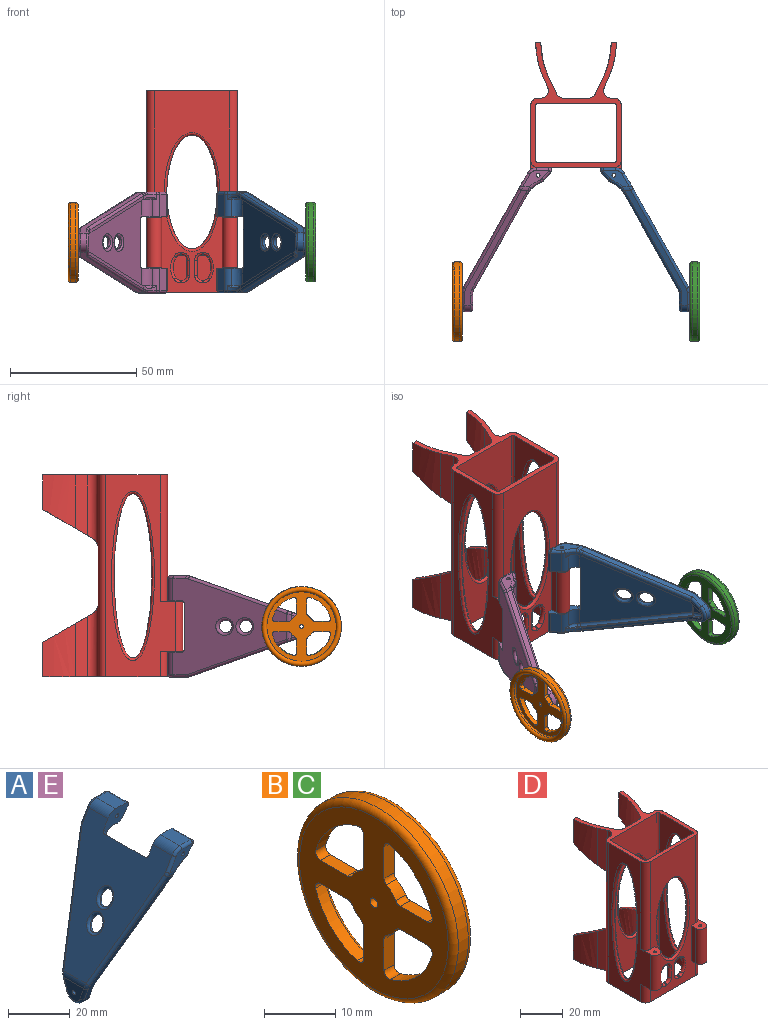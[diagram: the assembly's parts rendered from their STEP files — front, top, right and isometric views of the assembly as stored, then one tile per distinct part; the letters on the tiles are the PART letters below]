
ASSEMBLY  parts=5 mates=6
PART A: 94 faces, bbox 35.6x40.5x58 mm
  f0: cylinder r=3mm len=8.75mm, axis (0,1,0), area 25.5mm2, adj f1,f25,f29,f32,f38,f85
  f1: plane 8.75x3.29mm, normal (0.77,0,-0.64), area 37.5mm2, adj f0,f25,f52,f83
  f2: plane 8.75x4.95mm, normal (0,0,1), area 43.3mm2, adj f25,f31,f52,f79
  f3: cylinder r=3mm len=8.75mm, axis (0,1,0), area 25.5mm2, adj f4,f24,f28,f30,f40,f76
  f4: plane 8.75x3.29mm, normal (0.77,0,-0.64), area 37.5mm2, adj f3,f24,f55,f74
  f5: plane 8.75x4.95mm, normal (0,0,1), area 43.3mm2, adj f24,f37,f55,f70
  f6: plane 10.42x6.61mm, normal (0,-1,0), area 31.7mm2, adj f27,f34,f66,f68,f70,f74,f76,f78
  f7: plane 10.42x6.61mm, normal (0,1,0), area 31.7mm2, adj f26,f33,f75,f77,f79,f83,f85,f87
  f8: plane 40.52x33.68mm, normal (0.87,0,-0.49), area 800.5mm2, adj f23,f30,f32,f43,f46,f47,f53,f54
  f9: plane 37.92x21.33mm, normal (0.87,0,-0.49), area 53.6mm2, adj f22,f28,f36,f84
  f10: plane 38.87x21.87mm, normal (0.87,0,-0.49), area 54.9mm2, adj f11,f20,f29,f92,f93
  f11: plane 8.76x6.93mm, normal (1,0,0), area 15.1mm2, adj f10,f20,f21,f22,f36,f88,f90,f92
  f12: plane 45.38x38.33mm, normal (-0.87,0,0.49), area 1142.3mm2, adj f23,f24,f25,f31,f35,f37,f53,f54
  f13: plane 9.15x6.95mm, normal (-1,0,0), area 43.1mm2, adj f35,f56,f63,f65,f67
  f14: plane 45.39x24.79mm, normal (0,0.94,-0.33), area 113.4mm2, adj f15,f33,f67,f69,f71,f91,f92,f93
  f15: cylinder r=4mm len=7.55mm, axis (1,0,0), area 20.6mm2, adj f14,f16,f65,f90
  f16: plane 45.39x24.79mm, normal (0,-0.94,-0.33), area 113.5mm2, adj f15,f34,f61,f62,f63,f82,f84,f86
  f17: plane 2.99x1.2mm, normal (0,1,0), area 1.9mm2, adj f22,f28,f42,f44
  f18: plane 2.99x1.2mm, normal (0,-1,0), area 1.9mm2, adj f20,f29,f39,f41
  f19: plane 5.21x5.09mm, normal (1,0,0), area 15mm2, adj f47,f48,f50,f51,f56
  f20: plane 45.75x24.74mm, normal (0,-0.94,0.33), area 51.8mm2, adj f10,f11,f18,f21,f29,f41,f43,f48
  f21: cylinder r=2mm len=3.77mm, axis (1,0,0), area 5.3mm2, adj f11,f20,f22,f50
  f22: plane 45.75x24.74mm, normal (0,0.94,0.33), area 51.9mm2, adj f9,f11,f17,f21,f28,f36,f44,f46
  f23: cylinder r=7.5mm len=18.5mm, axis (0,1,0), area 40.8mm2, adj f8,f12,f53,f54
  f24: plane 11.33x7.37mm, normal (0,1,0), area 49mm2, adj f3,f4,f5,f12,f27,f30,f37,f54
  f25: plane 11.33x7.37mm, normal (0,-1,0), area 49mm2, adj f0,f1,f2,f12,f26,f31,f32,f52
  f26: cylinder r=0.75mm len=9.75mm, axis (0,-1,0), area 45.9mm2, adj f7,f25
  f27: cylinder r=0.75mm len=9.75mm, axis (0,-1,0), area 45.9mm2, adj f6,f24
  f28: cylinder r=10mm len=5.14mm, axis (0,1,0), area 8.4mm2, adj f3,f9,f17,f22,f40,f42,f78,f80
  f29: cylinder r=10mm len=5.14mm, axis (0,1,0), area 8.4mm2, adj f0,f10,f18,f20,f38,f39,f87,f89
  f30: cylinder r=4mm len=6.91mm, axis (0,1,0), area 34.9mm2, adj f3,f8,f24,f42,f44,f54
  f31: cylinder r=4mm len=8.75mm, axis (0,1,0), area 37mm2, adj f2,f12,f25,f77
  f32: cylinder r=4mm len=6.91mm, axis (0,1,0), area 34.9mm2, adj f0,f8,f25,f39,f41,f53
  f33: cylinder r=4mm len=3.32mm, axis (1,0,0), area 3.6mm2, adj f7,f14,f73,f89
  f34: cylinder r=4mm len=3.32mm, axis (-1,0,0), area 3.6mm2, adj f6,f16,f64,f80
  f35: cylinder r=4mm len=10.19mm, axis (0,1,0), area 19.8mm2, adj f12,f13,f61,f69
  f36: cylinder r=4mm len=1.96mm, axis (0,-1,0), area 2.4mm2, adj f9,f11,f22,f86
  f37: cylinder r=4mm len=8.75mm, axis (0,1,0), area 37mm2, adj f5,f12,f24,f68
  f38: torus R=4mm, axis (0,-1,0), area 1.4mm2, adj f0,f29,f39
  f39: torus R=3mm, axis (0,-1,0), area 6.2mm2, adj f18,f29,f32,f38,f41
  f40: torus R=4mm, axis (0,-1,0), area 1.4mm2, adj f3,f28,f42
  f41: bspline ~2.59x2.16mm, area 1.7mm2, adj f18,f20,f32,f39,f43
  f42: torus R=3mm, axis (0,-1,0), area 6.2mm2, adj f17,f28,f30,f40,f44
  f43: cylinder r=1mm len=41.27mm, axis (0.47,0.29,0.83), area 84.2mm2, adj f8,f20,f41,f45
  f44: bspline ~2.59x2.16mm, area 1.7mm2, adj f17,f22,f30,f42,f46
  f45: sphere r=1mm, area 0.4mm2, adj f43,f47,f48
  f46: cylinder r=1mm len=41.27mm, axis (-0.47,0.29,-0.83), area 84.2mm2, adj f8,f22,f44,f49
  f47: cylinder r=1mm len=5.09mm, axis (0,-1,0), area 2.6mm2, adj f8,f19,f45,f49
  f48: cylinder r=1mm len=4.88mm, axis (0,0.33,0.94), area 7.6mm2, adj f19,f20,f45,f50
  f49: sphere r=1mm, area 0.4mm2, adj f46,f47,f51
  f50: torus R=1mm, axis (-1,0,0), area 6.3mm2, adj f19,f21,f48,f51
  f51: cylinder r=1mm len=4.88mm, axis (0,0.33,-0.94), area 7.6mm2, adj f19,f22,f49,f50
  f52: cylinder r=1mm len=8.75mm, axis (0,1,0), area 19.9mm2, adj f1,f2,f25,f81
  f53: torus R=6.5mm, axis (0,-1,0), area 3.7mm2, adj f8,f12,f23,f25,f32
  f54: torus R=6.5mm, axis (0,-1,0), area 3.7mm2, adj f8,f12,f23,f24,f30
  f55: cylinder r=1mm len=8.75mm, axis (0,1,0), area 19.9mm2, adj f4,f5,f24,f72
  f56: cylinder r=0.75mm len=2mm, axis (-1,0,0), area 9.4mm2, adj f13,f19
  f57: bspline ~7x7mm, area 30.8mm2, adj f12,f58
  f58: bspline ~7x6.99mm, area 30.9mm2, adj f8,f57
  f59: bspline ~7x7mm, area 30.8mm2, adj f12,f60
  f60: bspline ~7x6.99mm, area 30.9mm2, adj f8,f59
  f61: bspline ~2.29x1.46mm, area 3.2mm2, adj f16,f35,f62,f63
  f62: cylinder r=1mm len=39.79mm, axis (0.47,-0.29,0.83), area 81.1mm2, adj f12,f16,f61,f64
  f63: cylinder r=1mm len=5.28mm, axis (0,-0.33,0.94), area 8.2mm2, adj f13,f16,f61,f65
  f64: bspline ~2.83x2.1mm, area 2.2mm2, adj f12,f34,f62,f66
  f65: torus R=3mm, axis (-1,0,0), area 14.1mm2, adj f13,f15,f63,f67
  f66: cylinder r=1mm len=5.57mm, axis (0.49,0,0.87), area 9.2mm2, adj f6,f12,f64,f68
  f67: cylinder r=1mm len=5.28mm, axis (0,-0.33,-0.94), area 8.2mm2, adj f13,f14,f65,f69
  f68: torus R=3mm, axis (0,-1,0), area 6mm2, adj f6,f37,f66,f70
  f69: bspline ~2.29x1.46mm, area 3.2mm2, adj f14,f35,f67,f71
  f70: cylinder r=1mm len=4.95mm, axis (1,0,0), area 7.8mm2, adj f5,f6,f68,f72
  f71: cylinder r=1mm len=39.79mm, axis (-0.47,-0.29,-0.83), area 81.1mm2, adj f12,f14,f69,f73
  f72: sphere r=1mm, area 2.6mm2, adj f55,f70,f74
  f73: bspline ~2.83x2.1mm, area 2.2mm2, adj f12,f33,f71,f75
  f74: cylinder r=1mm len=3.93mm, axis (-0.64,0,-0.77), area 6.7mm2, adj f4,f6,f72,f76
  f75: cylinder r=1mm len=5.57mm, axis (-0.49,0,-0.87), area 9.2mm2, adj f7,f12,f73,f77
  f76: torus R=2mm, axis (0,-1,0), area 2.1mm2, adj f3,f6,f74,f78
  f77: torus R=3mm, axis (0,-1,0), area 6mm2, adj f7,f31,f75,f79
  f78: torus R=11mm, axis (0,-1,0), area 7.4mm2, adj f6,f28,f76,f80
  f79: cylinder r=1mm len=4.95mm, axis (-1,0,0), area 7.8mm2, adj f2,f7,f77,f81
  f80: bspline ~3.6x2.99mm, area 2.1mm2, adj f28,f34,f78,f82
  f81: sphere r=1mm, area 2.6mm2, adj f52,f79,f83
  f82: bspline ~1.54x1.36mm, area 1.9mm2, adj f16,f28,f80,f84
  f83: cylinder r=1mm len=3.93mm, axis (0.64,0,0.77), area 6.7mm2, adj f1,f7,f81,f85
  f84: cylinder r=1mm len=38.14mm, axis (-0.47,0.29,-0.83), area 64mm2, adj f9,f16,f82,f86
  f85: torus R=2mm, axis (0,-1,0), area 2.1mm2, adj f0,f7,f83,f87
  f86: bspline ~3.56x2.2mm, area 3.6mm2, adj f16,f36,f84,f88
  f87: torus R=11mm, axis (0,-1,0), area 7.4mm2, adj f7,f29,f85,f89
  f88: cylinder r=1mm len=4.21mm, axis (0,0.33,-0.94), area 6.5mm2, adj f11,f16,f86,f90
  f89: bspline ~3.6x2.99mm, area 2.1mm2, adj f29,f33,f87,f91
  f90: torus R=3mm, axis (1,0,0), area 14.1mm2, adj f11,f15,f88,f92
  f91: bspline ~1.54x1.36mm, area 1.9mm2, adj f14,f29,f89,f93
  f92: cylinder r=1mm len=5.52mm, axis (0,0.33,0.94), area 8.4mm2, adj f10,f11,f14,f90,f93
  f93: cylinder r=1mm len=39.28mm, axis (0.47,0.29,0.83), area 65.8mm2, adj f10,f14,f91,f92
PART B: 39 faces, bbox 4x34.1x34.1 mm
  f0: plane 29.5x29.5mm, normal (-1,0,0), area 424.6mm2, adj f2,f5,f7,f8,f9,f10,f11,f12
  f1: cylinder r=15.75mm len=31.5mm, axis (-1,0,0), area 197.9mm2, adj f5,f6
  f2: cylinder r=0.75mm len=2mm, axis (-1,0,0), area 9.4mm2, adj f0,f3
  f3: plane 27.5x27.5mm, normal (1,0,0), area 335.1mm2, adj f2,f4,f7,f8,f9,f10,f11,f12
  f4: cylinder r=13.75mm len=27.5mm, axis (-1,0,0), area 86.4mm2, adj f3,f6
  f5: torus R=14.75mm, axis (1,0,0), area 151.9mm2, adj f0,f1
  f6: torus R=14.75mm, axis (1,0,0), area 291.2mm2, adj f1,f4
  f7: plane 5.39x2mm, normal (0,-1,0), area 10.8mm2, adj f0,f3,f11,f14
  f8: cylinder r=5mm len=2mm, axis (1,0,0), area 5.2mm2, adj f0,f3,f11,f12
  f9: plane 5.39x2mm, normal (0,0,-1), area 10.8mm2, adj f0,f3,f12,f13
  f10: cylinder r=12mm len=8.27mm, axis (1,0,0), area 24.4mm2, adj f0,f3,f13,f14
  f11: cylinder r=1mm len=2mm, axis (1,0,0), area 2.1mm2, adj f0,f3,f7,f8
  f12: cylinder r=1mm len=2mm, axis (1,0,0), area 2.1mm2, adj f0,f3,f8,f9
  f13: cylinder r=1mm len=2mm, axis (1,0,0), area 3.7mm2, adj f0,f3,f9,f10
  f14: cylinder r=1mm len=2mm, axis (1,0,0), area 3.7mm2, adj f0,f3,f7,f10
  f15: plane 5.39x2mm, normal (0,0,1), area 10.8mm2, adj f0,f3,f19,f22
  f16: cylinder r=5mm len=2mm, axis (1,0,0), area 5.2mm2, adj f0,f3,f19,f20
  f17: plane 5.39x2mm, normal (0,-1,0), area 10.8mm2, adj f0,f3,f20,f21
  f18: cylinder r=12mm len=8.27mm, axis (1,0,0), area 24.4mm2, adj f0,f3,f21,f22
  f19: cylinder r=1mm len=2mm, axis (1,0,0), area 2.1mm2, adj f0,f3,f15,f16
  f20: cylinder r=1mm len=2mm, axis (1,0,0), area 2.1mm2, adj f0,f3,f16,f17
  f21: cylinder r=1mm len=2mm, axis (1,0,0), area 3.7mm2, adj f0,f3,f17,f18
  f22: cylinder r=1mm len=2mm, axis (1,0,0), area 3.7mm2, adj f0,f3,f15,f18
  f23: plane 5.39x2mm, normal (0,1,0), area 10.8mm2, adj f0,f3,f27,f30
  f24: cylinder r=5mm len=2mm, axis (1,0,0), area 5.2mm2, adj f0,f3,f27,f28
  f25: plane 5.39x2mm, normal (0,0,1), area 10.8mm2, adj f0,f3,f28,f29
  f26: cylinder r=12mm len=8.27mm, axis (1,0,0), area 24.4mm2, adj f0,f3,f29,f30
  f27: cylinder r=1mm len=2mm, axis (1,0,0), area 2.1mm2, adj f0,f3,f23,f24
  f28: cylinder r=1mm len=2mm, axis (1,0,0), area 2.1mm2, adj f0,f3,f24,f25
  f29: cylinder r=1mm len=2mm, axis (1,0,0), area 3.7mm2, adj f0,f3,f25,f26
  f30: cylinder r=1mm len=2mm, axis (1,0,0), area 3.7mm2, adj f0,f3,f23,f26
  f31: plane 5.39x2mm, normal (0,0,-1), area 10.8mm2, adj f0,f3,f35,f38
  f32: cylinder r=5mm len=2mm, axis (1,0,0), area 5.2mm2, adj f0,f3,f35,f36
  f33: plane 5.39x2mm, normal (0,1,0), area 10.8mm2, adj f0,f3,f36,f37
  f34: cylinder r=12mm len=8.27mm, axis (1,0,0), area 24.4mm2, adj f0,f3,f37,f38
  f35: cylinder r=1mm len=2mm, axis (1,0,0), area 2.1mm2, adj f0,f3,f31,f32
  f36: cylinder r=1mm len=2mm, axis (1,0,0), area 2.1mm2, adj f0,f3,f32,f33
  f37: cylinder r=1mm len=2mm, axis (1,0,0), area 3.7mm2, adj f0,f3,f33,f34
  f38: cylinder r=1mm len=2mm, axis (1,0,0), area 3.7mm2, adj f0,f3,f31,f34
PART C: same geometry as B
PART D: 100 faces, bbox 36.6x56.1x80.6 mm
  f0: extruded ~40.69x5.73mm, area 52.2mm2, adj f26,f45,f49,f83,f86,f87
  f1: plane 80x30mm, normal (0,-1,0), area 1311.5mm2, adj f33,f34,f36,f38,f39,f41,f43,f44
  f2: plane 80x30mm, normal (0,1,0), area 1431.5mm2, adj f33,f34,f67,f68,f69,f70,f71,f72
  f3: plane 23.94x4.82mm, normal (0.92,-0.4,0), area 118.5mm2, adj f11,f33,f51,f58
  f4: plane 23.94x4.82mm, normal (0.92,-0.4,0), area 118.5mm2, adj f12,f34,f48,f53
  f5: plane 25.42x7.29mm, normal (-0.91,0.42,0), area 186.8mm2, adj f15,f33,f51,f52,f59,f89
  f6: plane 25.42x7.29mm, normal (-0.91,0.42,0), area 186.8mm2, adj f16,f34,f47,f48,f54,f84
  f7: plane 23.94x4.82mm, normal (-0.92,-0.4,0), area 118.5mm2, adj f19,f33,f50,f55
  f8: plane 23.94x4.82mm, normal (-0.92,-0.4,0), area 118.5mm2, adj f20,f34,f46,f57
  f9: plane 25.42x7.29mm, normal (0.91,0.42,0), area 186.8mm2, adj f21,f33,f49,f50,f60,f86
  f10: plane 25.42x7.29mm, normal (0.91,0.42,0), area 186.8mm2, adj f22,f34,f45,f46,f56,f83
  f11: extruded ~21.15x12.99mm, area 231.5mm2, adj f3,f13,f33,f51
  f12: extruded ~21.15x12.99mm, area 231.5mm2, adj f4,f14,f34,f48
  f13: plane 13.65x2mm, normal (0,1,0), area 27.3mm2, adj f11,f15,f33,f51
  f14: plane 13.65x2mm, normal (0,1,0), area 27.3mm2, adj f12,f16,f34,f48
  f15: extruded ~21.15x12.99mm, area 232mm2, adj f5,f13,f33,f51
  f16: extruded ~21.15x12.99mm, area 232mm2, adj f6,f14,f34,f48
  f17: plane 13.65x2mm, normal (0,1,0), area 27.3mm2, adj f19,f21,f33,f50
  f18: plane 13.65x2mm, normal (0,1,0), area 27.3mm2, adj f20,f22,f34,f46
  f19: extruded ~21.15x12.99mm, area 231.5mm2, adj f7,f17,f33,f50
  f20: extruded ~21.15x12.99mm, area 231.5mm2, adj f8,f18,f34,f46
  f21: extruded ~21.15x12.99mm, area 232mm2, adj f9,f17,f33,f50
  f22: extruded ~21.15x12.99mm, area 232mm2, adj f10,f18,f34,f46
  f23: extruded ~40.69x5.73mm, area 52.2mm2, adj f27,f47,f52,f84,f87,f89
  f24: plane 18.98x10.01mm, normal (0,1,0), area 173mm2, adj f34,f54,f56,f85
  f25: plane 18.98x10.01mm, normal (0,1,0), area 173mm2, adj f33,f59,f60,f88
  f26: plane 80x6.22mm, normal (0,1,0), area 178.5mm2, adj f0,f33,f34,f45,f49,f55,f57,f63
  f27: plane 80x6.22mm, normal (0,1,0), area 178.5mm2, adj f23,f33,f34,f47,f52,f53,f58,f66
  f28: plane 80x27.5mm, normal (-1,0,0), area 926.6mm2, adj f33,f34,f35,f38,f39,f62,f63,f64
  f29: plane 80x21.5mm, normal (1,0,0), area 806.6mm2, adj f33,f34,f92,f96,f99
  f30: plane 80x30mm, normal (0,-1,0), area 1584mm2, adj f33,f34,f87,f96,f97
  f31: plane 80x21.5mm, normal (-1,0,0), area 806.6mm2, adj f33,f34,f95,f97,f98
  f32: plane 80x27.5mm, normal (1,0,0), area 926.6mm2, adj f33,f34,f40,f43,f44,f61,f65,f66
  f33: plane 49.5x36mm, normal (0,0,1), area 336.5mm2, adj f1,f2,f3,f5,f7,f9,f11,f13
  f34: plane 49.5x36mm, normal (0,0,-1), area 336.5mm2, adj f1,f2,f4,f6,f8,f10,f12,f14
  f35: cylinder r=3mm len=20mm, axis (0,0,1), area 188.5mm2, adj f28,f36,f38,f39
  f36: plane 20x3mm, normal (1,0,0), area 60mm2, adj f1,f35,f38,f39
  f37: cylinder r=0.75mm len=20mm, axis (0,0,1), area 94.2mm2, adj f38,f39
  f38: plane 9x6mm, normal (0,0,-1), area 32.3mm2, adj f1,f28,f35,f36,f37,f62
  f39: plane 9x6mm, normal (0,0,1), area 32.3mm2, adj f1,f28,f35,f36,f37,f64
  f40: cylinder r=3mm len=20mm, axis (0,0,1), area 188.5mm2, adj f32,f41,f43,f44
  f41: plane 20x3mm, normal (-1,0,0), area 60mm2, adj f1,f40,f43,f44
  f42: cylinder r=0.75mm len=20mm, axis (0,0,1), area 94.2mm2, adj f43,f44
  f43: plane 9x6mm, normal (0,0,-1), area 32.3mm2, adj f1,f32,f40,f41,f42,f61
  f44: plane 9x6mm, normal (0,0,1), area 32.3mm2, adj f1,f32,f40,f41,f42,f65
  f45: cylinder r=5mm len=6.19mm, axis (-1,0,0), area 21.1mm2, adj f0,f10,f26,f46,f57,f83
  f46: plane 20.05x11.81mm, normal (0,0.5,0.87), area 48mm2, adj f8,f10,f18,f20,f22,f45,f57
  f47: cylinder r=5mm len=6.19mm, axis (-1,0,0), area 21.1mm2, adj f6,f23,f27,f48,f53,f84
  f48: plane 20.04x11.8mm, normal (0,0.5,0.87), area 48mm2, adj f4,f6,f12,f14,f16,f47,f53
  f49: cylinder r=5mm len=6.19mm, axis (-1,0,0), area 21.1mm2, adj f0,f9,f26,f50,f55,f86
  f50: plane 20.04x11.8mm, normal (0,0.5,-0.87), area 48mm2, adj f7,f9,f17,f19,f21,f49,f55
  f51: plane 20.03x11.79mm, normal (0,0.5,-0.87), area 48mm2, adj f3,f5,f11,f13,f15,f52,f58
  f52: cylinder r=5mm len=6.19mm, axis (-1,0,0), area 21.1mm2, adj f5,f23,f27,f51,f58,f89
  f53: cylinder r=3mm len=29.24mm, axis (0,0,1), area 156.2mm2, adj f4,f27,f34,f47,f48
  f54: cylinder r=3mm len=25.26mm, axis (0,0,1), area 75.3mm2, adj f6,f24,f34,f84
  f55: cylinder r=3mm len=29.24mm, axis (0,0,-1), area 156.2mm2, adj f7,f26,f33,f49,f50
  f56: cylinder r=3mm len=25.26mm, axis (0,0,1), area 75.3mm2, adj f10,f24,f34,f83
  f57: cylinder r=3mm len=29.24mm, axis (0,0,-1), area 156.2mm2, adj f8,f26,f34,f45,f46
  f58: cylinder r=3mm len=29.24mm, axis (0,0,1), area 156.2mm2, adj f3,f27,f33,f51,f52
  f59: cylinder r=3mm len=25.26mm, axis (0,0,1), area 75.3mm2, adj f5,f25,f33,f89
  f60: cylinder r=3mm len=25.26mm, axis (0,0,1), area 75.3mm2, adj f9,f25,f33,f86
  f61: cylinder r=3mm len=10mm, axis (0,0,1), area 47.1mm2, adj f1,f32,f34,f43
  f62: cylinder r=3mm len=10mm, axis (0,0,-1), area 47.1mm2, adj f1,f28,f34,f38
  f63: cylinder r=3mm len=80mm, axis (0,0,1), area 377mm2, adj f26,f28,f33,f34
  f64: cylinder r=3mm len=50mm, axis (0,0,-1), area 235.6mm2, adj f1,f28,f33,f39
  f65: cylinder r=3mm len=50mm, axis (0,0,1), area 235.6mm2, adj f1,f32,f33,f44
  f66: cylinder r=3mm len=80mm, axis (0,0,-1), area 377mm2, adj f27,f32,f33,f34
  f67: cylinder r=1mm len=6mm, axis (0,0,1), area 18.8mm2, adj f1,f2,f68,f69
  f68: torus R=3mm, axis (0,1,0), area 11.7mm2, adj f1,f2,f67,f70
  f69: torus R=3mm, axis (0,1,0), area 11.7mm2, adj f1,f2,f67,f71
  f70: cylinder r=1mm len=2mm, axis (1,0,0), area 1.9mm2, adj f1,f2,f68,f72
  f71: cylinder r=1mm len=2mm, axis (-1,0,0), area 1.9mm2, adj f1,f2,f69,f73
  f72: torus R=3mm, axis (0,1,0), area 7.4mm2, adj f1,f2,f70,f74
  f73: torus R=3mm, axis (0,1,0), area 7.4mm2, adj f1,f2,f71,f74
  f74: torus R=8.5mm, axis (0,1,0), area 28.5mm2, adj f1,f2,f72,f73
  f75: torus R=8.5mm, axis (0,1,0), area 28.5mm2, adj f1,f2,f76,f77
  f76: torus R=3mm, axis (0,1,0), area 7.4mm2, adj f1,f2,f75,f78
  f77: torus R=3mm, axis (0,1,0), area 7.4mm2, adj f1,f2,f75,f79
  f78: cylinder r=1mm len=2mm, axis (1,0,0), area 1.9mm2, adj f1,f2,f76,f80
  f79: cylinder r=1mm len=2mm, axis (-1,0,0), area 1.9mm2, adj f1,f2,f77,f81
  f80: torus R=3mm, axis (0,1,0), area 11.7mm2, adj f1,f2,f78,f82
  f81: torus R=3mm, axis (0,1,0), area 11.7mm2, adj f1,f2,f79,f82
  f82: cylinder r=1mm len=6mm, axis (0,0,-1), area 18.8mm2, adj f1,f2,f80,f81
  f83: bspline ~7.97x4.36mm, area 7.7mm2, adj f0,f10,f45,f56,f85
  f84: bspline ~7.97x4.36mm, area 7.7mm2, adj f6,f23,f47,f54,f85
  f85: bspline ~12.09x4.33mm, area 16.4mm2, adj f24,f83,f84,f87
  f86: bspline ~7.97x4.36mm, area 7.7mm2, adj f0,f9,f49,f60,f88
  f87: bspline ~47.01x22.01mm, area 169.9mm2, adj f0,f23,f30,f85,f88
  f88: bspline ~12.09x4.33mm, area 16.4mm2, adj f25,f86,f87,f89
  f89: bspline ~7.97x4.36mm, area 7.7mm2, adj f5,f23,f52,f59,f88
  f90: bspline ~47.01x22.01mm, area 169.9mm2, adj f2,f91
  f91: bspline ~46.93x21.99mm, area 169.9mm2, adj f1,f90
  f92: bspline ~67x17.01mm, area 220.8mm2, adj f29,f93
  f93: bspline ~66.64x17mm, area 220.8mm2, adj f28,f92
  f94: bspline ~67x17.01mm, area 220.8mm2, adj f32,f95
  f95: bspline ~66.64x17mm, area 220.8mm2, adj f31,f94
  f96: cylinder r=1mm len=80mm, axis (0,0,-1), area 125.7mm2, adj f29,f30,f33,f34
  f97: cylinder r=1mm len=80mm, axis (0,0,1), area 125.7mm2, adj f30,f31,f33,f34
  f98: cylinder r=1mm len=80mm, axis (0,0,-1), area 125.7mm2, adj f2,f31,f33,f34
  f99: cylinder r=1mm len=80mm, axis (0,0,1), area 125.7mm2, adj f2,f29,f33,f34
PART E: same geometry as A
PLACE A rot(axis=(0,0.71,0.71),180deg) t=(31.01,-13.96,-17.19)mm
PLACE B rot(axis=(0,1,0),180deg) t=(-30.99,-63.96,-17.34)mm
PLACE C t=(63.01,-63.96,-17.19)mm
PLACE D t=(16.01,2.79,2.71)mm
PLACE E rot(axis=(-1,0,0),90deg) t=(1.01,-13.96,-17.34)mm
MATE cylindrical A.f26 <-> D.f40  axis (0,0,-1) through (31.01,-13.96,-37.19)mm
MATE planar C.f0 <-> A.f13  axis (-1,0,0) through (61.01,-61.96,-11.99)mm
MATE cylindrical C.f1 <-> A.f56  axis (-1,0,0) through (63.01,-63.96,-17.19)mm
MATE cylindrical B.f1 <-> E.f56  axis (1,0,0) through (-29.99,-63.96,-17.34)mm
MATE cylindrical E.f26 <-> D.f35  axis (0,0,1) through (1.01,-13.96,-7.09)mm
MATE planar B.f0 <-> E.f13  axis (1,0,0) through (-28.99,-61.96,-22.53)mm
